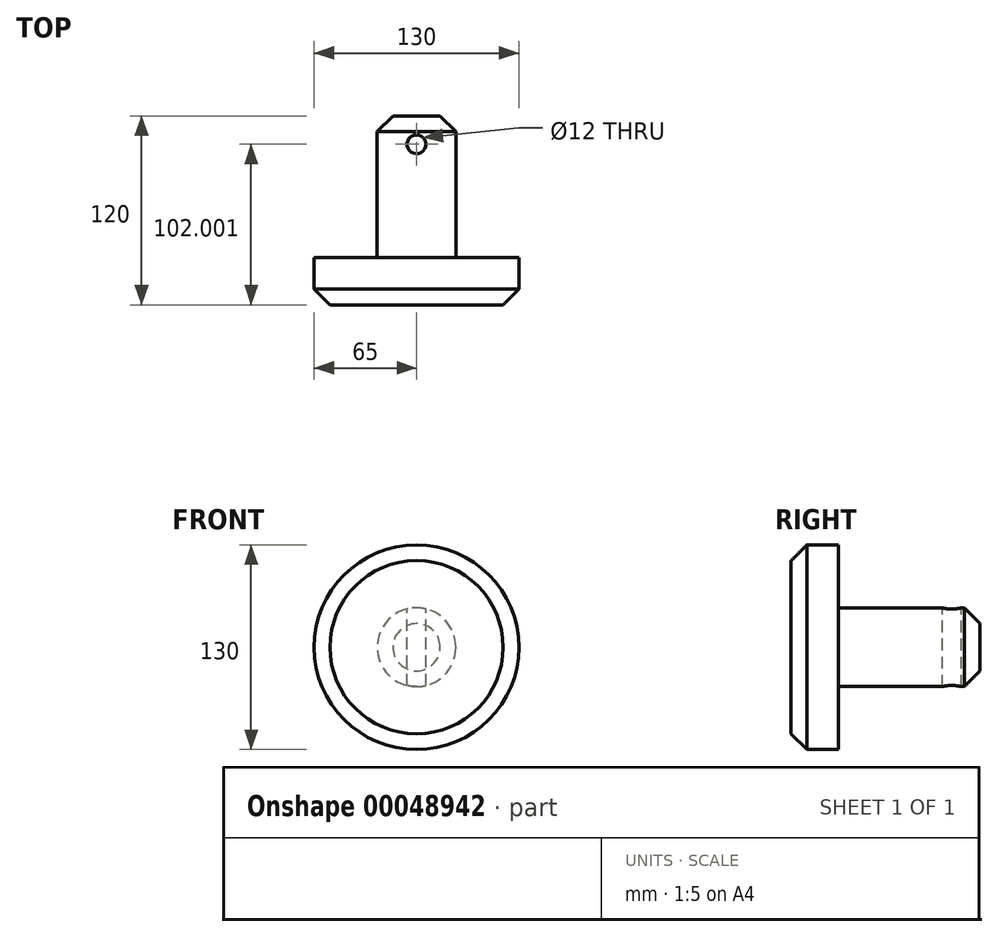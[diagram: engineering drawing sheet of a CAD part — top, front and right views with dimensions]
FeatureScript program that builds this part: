
annotation { "Feature Type Name" : "Feature", "Feature Type Description" : "" }
export const myFeature = defineFeature(function(context is Context, id is Id, definition is map)
    precondition{}
    {
        {
            var Q0;
            Q0=qCreatedBy(makeId("Right.planeOp"),FACE);
            var sketch = newSketch(context, id + "F0", { "sketchPlane" : qUnion([Q0])});
            skLineSegment(sketch, "E0", {"start": v(-138.62, -15.62) * mm, "end": v(-18.62, -15.62) * mm});
            skLineSegment(sketch, "E1", {"start": v(-18.62, -15.62) * mm, "end": v(-18.62, 9.38) * mm});
            skLineSegment(sketch, "E2", {"start": v(-18.62, 9.38) * mm, "end": v(-108.62, 9.38) * mm});
            skLineSegment(sketch, "E3", {"start": v(-108.62, 9.38) * mm, "end": v(-108.62, 49.38) * mm});
            skLineSegment(sketch, "E4", {"start": v(-108.62, 49.38) * mm, "end": v(-138.62, 49.38) * mm});
            skLineSegment(sketch, "E5", {"start": v(-138.62, 49.38) * mm, "end": v(-138.62, -15.62) * mm});
            skLineSegment(sketch, "E6", {"start": v(-108.62, -23.35) * mm, "end": v(-36.62, -23.35) * mm, "construction": true});
            skLineSegment(sketch, "E7", {"start": v(-36.62, -23.35) * mm, "end": v(-36.62, -15.62) * mm, "construction": true});
            skSolve(sketch);
        }
        {
            var Q0;
            Q0=makeQuery(id+"F0.imprint","IMPRINT",FACE,{"disambiguationData":[TD([[makeQuery(id+"F0.imprint","IMPRINT",EDGE,{"derivedFrom":sQuery(id+"F0.wireOp",EDGE,"E0")}),1.0]])]});
            var Q1;
            Q1=sQuery(id+"F0.wireOp",EDGE,"E0");
            revolve(context, id + "F1", {"entities" : qUnion([Q0]), "axis" : qUnion([Q1]), "revolveType" : RevolveType.FULL});
        }
        {
            var Q0;
            Q0=makeQuery(id+"F1.opRevolve","SWEPT_EDGE",EDGE,{"disambiguationData":[OSD([sQuery(id+"F0.wireOp",EDGE,"E1"),sQuery(id+"F0.wireOp",EDGE,"E2")])]});
            chamfer(context, id + "F2", {"entities" : qUnion([Q0]), "chamferType" : ChamferType.OFFSET_ANGLE, "width" : 10 * mm, "oppositeDirection" : false, "angle" : 45 * degree, "tangentPropagation" : true});
        }
        {
            var Q0;
            Q0=makeQuery(id+"F1.opRevolve","SWEPT_EDGE",EDGE,{"disambiguationData":[OSD([sQuery(id+"F0.wireOp",EDGE,"E4"),sQuery(id+"F0.wireOp",EDGE,"E5")])]});
            chamfer(context, id + "F3", {"entities" : qUnion([Q0]), "chamferType" : ChamferType.OFFSET_ANGLE, "width" : 10 * mm, "oppositeDirection" : false, "angle" : 45 * degree, "tangentPropagation" : true});
        }
        {
            var Q0;
            Q0=qCreatedBy(makeId("Top.planeOp"),FACE);
            var sketch = newSketch(context, id + "F4", { "sketchPlane" : qUnion([Q0])});
            skLineSegment(sketch, "E8", {"start": v(28.66, -108.62) * mm, "end": v(28.66, -36.62) * mm, "construction": true});
            skLineSegment(sketch, "E9", {"start": v(28.66, -108.62) * mm, "end": v(28.66, -108.62) * mm});
            skLineSegment(sketch, "E10", {"start": v(28.66, -36.62) * mm, "end": v(0, -36.62) * mm, "construction": true});
            skCircle(sketch, "E11", {"center": v(0, -36.62) * mm, "radius": 6 * mm});
            skSolve(sketch);
        }
        {
            var Q0;
            Q0 = qSketchRegion(id + "F4", true);
            extrude(context, id + "F5", {"entities" : qUnion([Q0]), "operationType" : NewBodyOperationType.REMOVE, "endBound" : BoundingType.THROUGH_ALL, "oppositeDirection" : true, "depth" : 25 * mm, "hasSecondDirection" : true, "secondDirectionBound" : SecondDirectionBoundingType.THROUGH_ALL, "secondDirectionOppositeDirection" : false, "secondDirectionDepth" : 25 * mm});
        }
    });
